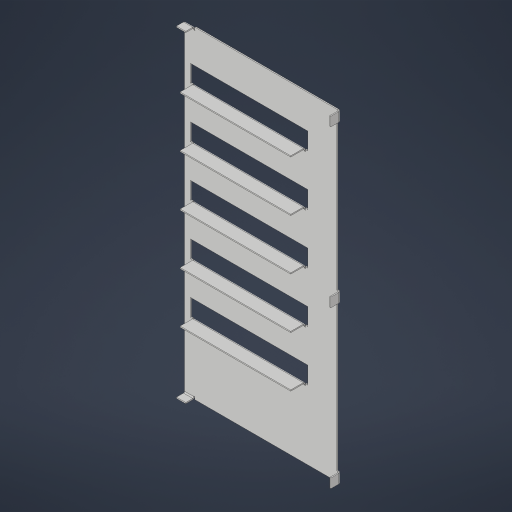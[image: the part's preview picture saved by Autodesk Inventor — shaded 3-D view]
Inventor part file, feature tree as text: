
AUTODESK INVENTOR PART (.ipt)
format: ipt  version: 2023.4 (Build 274418000, 418)  size: 506,880 bytes
history: native  units: in
note: dims shown in document units (in); Inventor stores cm internally (conversion verified against a paired STEP export)
features: sheet_metal_op x12, sketch x6, other x6, pattern_linear x1, extrude x1, projected_geometry x1
ambient origin geometry x8: Origin, YZ Plane, XZ Plane, XY Plane, X Axis, Y Axis, Z Axis, Center Point
bodies: Solid1 (feature_tree)
feature tree (27):
  sheet_metal_op  "Face1"
  sketch  "Sketch2"  dims[d1=35.0in]
  sheet_metal_op  "Face2"
  sheet_metal_op  "Fold1"
  sheet_metal_op  "Fold2"
  sketch  "Sketch3"  dims[d2=0.12in]
  sheet_metal_op  "Fold4"
  pattern_linear  "Rectangular Pattern1"  Spacing1=1.0in  [1 undecoded]
  extrude  "Extrusion1"  Depth=1.0in
  sheet_metal_op  "Flange1"
  sheet_metal_op  "Flange2"
  sketch  "Sketch1"  dims[d0=16.5in]
  other  "Plate1"
  other  "Plate2"
  sheet_metal_op  "Bend1"
  sketch  "Sketch4"  dims[d3=1.25in]
  sketch  "Sketch5"  dims[d4=1.0in]
  other  "Plate3"
  sheet_metal_op  "Bend2"
  sheet_metal_op  "Corner1"
  sketch  "Sketch6"  dims[d5=0.25in d6=1.0in d7=1.0in d8=1.25in d9=1.0in d10=0.25in d11=0.12in d12=0.12in d13=0.06in d14=0.24in d15=0.12in d16=0.12in d17=0.06in d18=0.24in d19=0.12in d20=90.0deg d21=0.12in d22=0.12in d23=0.06in d24=0.24in d25=0.12in d26=90.0deg d27=0.12in d28=5.5in d29=1.5in d30=12.0in d31=1.0in d32=0.375in d33=0.12in d34=0.0in d41=0.12in d42=0.06in d43=0.24in d44=0.12in d45=90.0deg d46=0.12in d47=1.9685in d49=5.5in d50=1.0in d51=0.0in d52=0.12in d53=0.06in d54=0.24in d55=0.12in d56=1.0in d57=0.0in d58=1.0in d59=90.0deg d60=0.12in d61=0.48in d62=0.12in d63=0.12in d64=0.12in d65=0.06in d66=0.24in d67=0.12in d68=1.0in d69=0.0in d70=1.0in d71=90.0deg d72=0.12in d73=0.48in d74=0.12in d75=0.12in]
  other  "Plate4"
  sheet_metal_op  "Bend3"
  sheet_metal_op  "Corner2"
  other  "Cut1"
  projected_geometry  "Project Cut Edges1"
  other  "Definition1"
note: 1 required parameter value undecoded (feature->parameter linkage not recoverable at this tier; creation-order binding heuristic only, values carry confidence <= 0.55)
